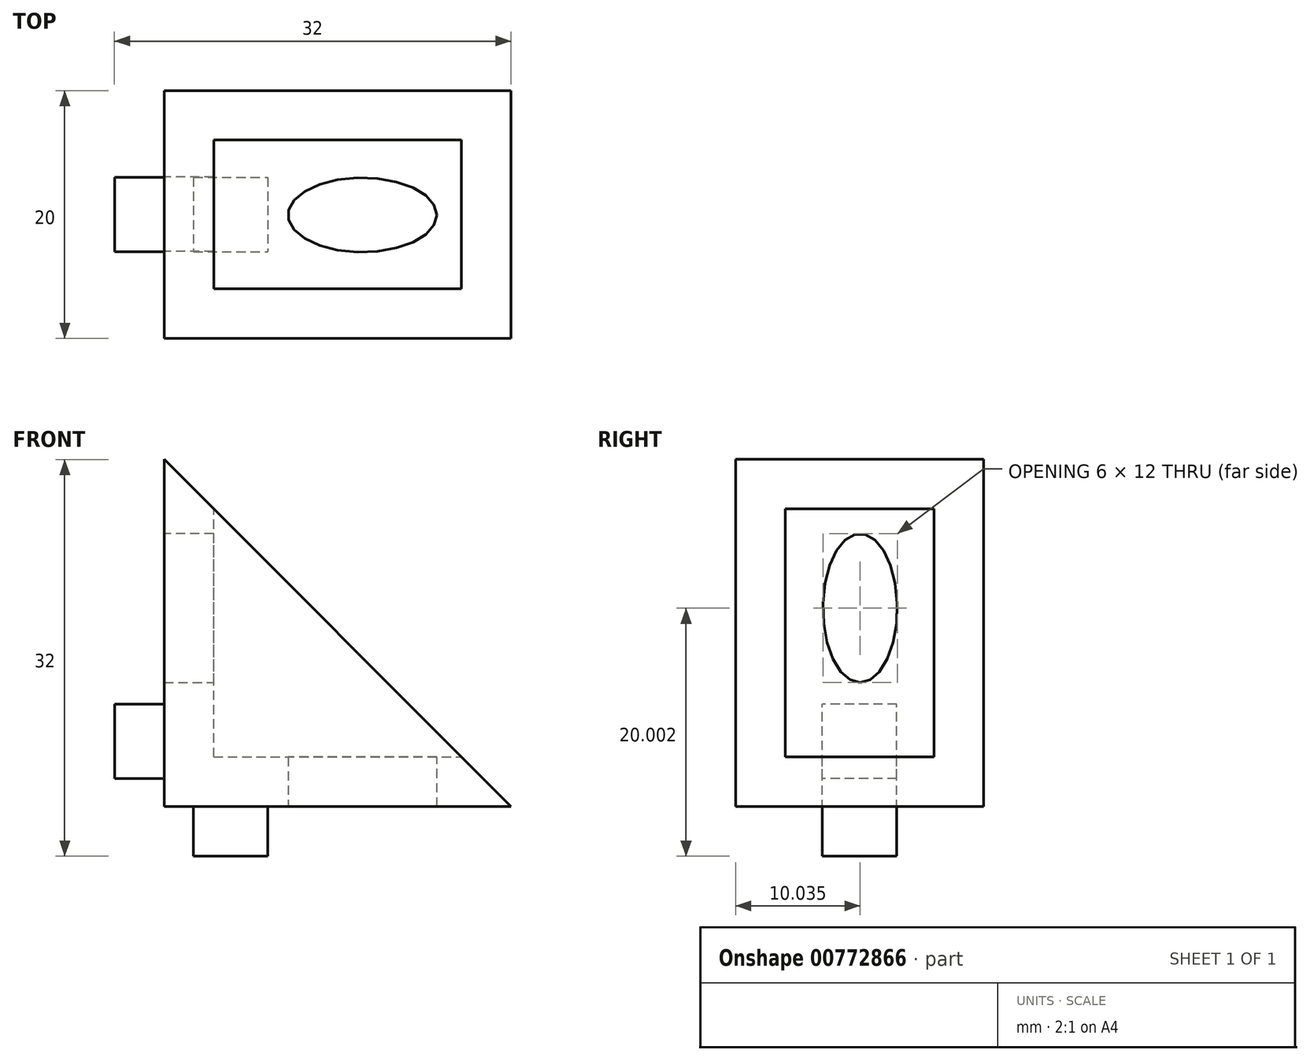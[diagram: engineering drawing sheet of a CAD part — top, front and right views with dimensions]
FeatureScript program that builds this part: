
annotation { "Feature Type Name" : "Feature", "Feature Type Description" : "" }
export const myFeature = defineFeature(function(context is Context, id is Id, definition is map)
    precondition{}
    {
        {
            var Q0;
            Q0=qCreatedBy(makeId("Front.planeOp"),FACE);
            var sketch = newSketch(context, id + "F0", { "sketchPlane" : qUnion([Q0])});
            skLineSegment(sketch, "E0.bottom", {"start": v(-14.58, 14.66) * mm, "end": v(13.42, 14.66) * mm});
            skLineSegment(sketch, "E0.top", {"start": v(-14.58, -13.34) * mm, "end": v(13.42, -13.34) * mm});
            skLineSegment(sketch, "E0.left", {"start": v(-14.58, 14.66) * mm, "end": v(-14.58, -13.34) * mm});
            skLineSegment(sketch, "E0.right", {"start": v(13.42, 14.66) * mm, "end": v(13.42, -13.34) * mm});
            skSolve(sketch);
        }
        {
            var Q0;
            Q0 = qSketchRegion(id + "F0", true);
            extrude(context, id + "F1", {"entities" : qUnion([Q0]), "depth" : 20 * mm, "offsetDistance" : 25 * mm});
        }
        {
            var Q0;
            Q0=makeQuery(id+"F1.opExtrude","SWEPT_FACE",FACE,{"disambiguationData":[OSD([sQuery(id+"F0.wireOp",EDGE,"E0.bottom")])]});
            var sketch = newSketch(context, id + "F2", { "sketchPlane" : qUnion([Q0])});
            skLineSegment(sketch, "E1.bottom", {"start": v(-10.58, -16) * mm, "end": v(9.42, -16) * mm});
            skLineSegment(sketch, "E1.top", {"start": v(-10.58, -4) * mm, "end": v(9.42, -4) * mm});
            skLineSegment(sketch, "E1.left", {"start": v(-10.58, -16) * mm, "end": v(-10.58, -4) * mm});
            skLineSegment(sketch, "E1.right", {"start": v(9.42, -16) * mm, "end": v(9.42, -4) * mm});
            skSolve(sketch);
        }
        {
            var Q0;
            Q0 = qSketchRegion(id + "F2", true);
            extrude(context, id + "F3", {"entities" : qUnion([Q0]), "operationType" : NewBodyOperationType.REMOVE, "oppositeDirection" : true, "depth" : 24 * mm, "offsetDistance" : 25 * mm});
        }
        {
            var Q0;
            Q0=makeQuery(id+"F1.opExtrude","SWEPT_FACE",FACE,{"disambiguationData":[OSD([sQuery(id+"F0.wireOp",EDGE,"E0.right")])]});
            var sketch = newSketch(context, id + "F4", { "sketchPlane" : qUnion([Q0])});
            skLineSegment(sketch, "E2.bottom", {"start": v(-16, 10.66) * mm, "end": v(-4, 10.66) * mm});
            skLineSegment(sketch, "E2.top", {"start": v(-16, -9.34) * mm, "end": v(-4, -9.34) * mm});
            skLineSegment(sketch, "E2.left", {"start": v(-16, 10.66) * mm, "end": v(-16, -9.34) * mm});
            skLineSegment(sketch, "E2.right", {"start": v(-4, 10.66) * mm, "end": v(-4, -9.34) * mm});
            skSolve(sketch);
        }
        {
            var Q0;
            Q0 = qSketchRegion(id + "F4", true);
            extrude(context, id + "F5", {"entities" : qUnion([Q0]), "operationType" : NewBodyOperationType.REMOVE, "oppositeDirection" : true, "depth" : 24 * mm, "offsetDistance" : 25 * mm});
        }
        {
            var Q0;
            Q0=makeQuery(id+"F1.opExtrude","CAP_FACE",FACE,{"disambiguationData":[OSD([sQuery(id+"F0.wireOp",EDGE,"E0.bottom"),sQuery(id+"F0.wireOp",EDGE,"E0.top"),sQuery(id+"F0.wireOp",EDGE,"E0.left"),sQuery(id+"F0.wireOp",EDGE,"E0.right")])],"isStart":false});
            var sketch = newSketch(context, id + "F6", { "sketchPlane" : qUnion([Q0])});
            skLineSegment(sketch, "E3", {"start": v(-14.58, 14.66) * mm, "end": v(13.42, -13.34) * mm});
            skLineSegment(sketch, "E4", {"start": v(13.42, -13.34) * mm, "end": v(13.42, 14.66) * mm});
            skLineSegment(sketch, "E5", {"start": v(13.42, 14.66) * mm, "end": v(-14.58, 14.66) * mm});
            skSolve(sketch);
        }
        {
            var Q0;
            Q0 = qSketchRegion(id + "F6", true);
            extrude(context, id + "F7", {"entities" : qUnion([Q0]), "operationType" : NewBodyOperationType.REMOVE, "endBound" : BoundingType.THROUGH_ALL, "oppositeDirection" : true, "depth" : 25 * mm, "offsetDistance" : 25 * mm});
        }
        {
            var Q0;
            Q0=makeQuery(id+"F5.boolean.opBoolean","MERGE",FACE,{"derivedFrom":[makeQuery(id+"F3.boolean.opBoolean","COPY",FACE,{"derivedFrom":makeQuery(id+"F3.opExtrude","CAP_FACE",FACE,{"disambiguationData":[OSD([sQuery(id+"F2.wireOp",EDGE,"E1.bottom"),sQuery(id+"F2.wireOp",EDGE,"E1.top"),sQuery(id+"F2.wireOp",EDGE,"E1.left"),sQuery(id+"F2.wireOp",EDGE,"E1.right")])],"isStart":false})}),makeQuery(id+"F5.opExtrude","SWEPT_FACE",FACE,{"disambiguationData":[OSD([sQuery(id+"F4.wireOp",EDGE,"E2.top")])]})]});
            var sketch = newSketch(context, id + "F8", { "sketchPlane" : qUnion([Q0])});
            skEllipse(sketch, "E6", {"center": v(1.42, -10.03) * mm, "majorRadius": 6 * mm, "minorRadius": 3 * mm, "majorAxis": v(1, 0)});
            skSolve(sketch);
        }
        {
            var Q0;
            Q0 = qSketchRegion(id + "F8", true);
            extrude(context, id + "F9", {"entities" : qUnion([Q0]), "operationType" : NewBodyOperationType.REMOVE, "endBound" : BoundingType.THROUGH_ALL, "oppositeDirection" : true, "depth" : 25 * mm, "offsetDistance" : 25 * mm});
        }
        {
            var Q0;
            Q0=makeQuery(id+"F3.boolean.opBoolean","COPY",FACE,{"derivedFrom":makeQuery(id+"F3.opExtrude","SWEPT_FACE",FACE,{"disambiguationData":[OSD([sQuery(id+"F2.wireOp",EDGE,"E1.left")])]})});
            var sketch = newSketch(context, id + "F10", { "sketchPlane" : qUnion([Q0])});
            skEllipse(sketch, "E7", {"center": v(-9.97, 2.66) * mm, "majorRadius": 6 * mm, "minorRadius": 3 * mm, "majorAxis": v(0, -1)});
            skSolve(sketch);
        }
        {
            var Q0;
            Q0 = qSketchRegion(id + "F10", true);
            extrude(context, id + "F11", {"entities" : qUnion([Q0]), "operationType" : NewBodyOperationType.REMOVE, "endBound" : BoundingType.THROUGH_ALL, "oppositeDirection" : true, "depth" : 25 * mm, "offsetDistance" : 25 * mm});
        }
        {
            var Q0;
            Q0=makeQuery(id+"F1.opExtrude","SWEPT_FACE",FACE,{"disambiguationData":[OSD([sQuery(id+"F0.wireOp",EDGE,"E0.left")])]});
            var sketch = newSketch(context, id + "F12", { "sketchPlane" : qUnion([Q0])});
            skLineSegment(sketch, "E8.bottom", {"start": v(7, -11.06) * mm, "end": v(13, -11.06) * mm});
            skLineSegment(sketch, "E8.top", {"start": v(7, -5.06) * mm, "end": v(13, -5.06) * mm});
            skLineSegment(sketch, "E8.left", {"start": v(7, -11.06) * mm, "end": v(7, -5.06) * mm});
            skLineSegment(sketch, "E8.right", {"start": v(13, -11.06) * mm, "end": v(13, -5.06) * mm});
            skSolve(sketch);
        }
        {
            var Q0;
            Q0=makeQuery(id+"F12.imprint","IMPRINT",FACE,{"disambiguationData":[TD([[makeQuery(id+"F12.imprint","IMPRINT",EDGE,{"derivedFrom":sQuery(id+"F12.wireOp",EDGE,"E8.bottom")}),1.0]])]});
            extrude(context, id + "F13", {"entities" : qUnion([Q0]), "operationType" : NewBodyOperationType.ADD, "depth" : 4 * mm, "offsetDistance" : 25 * mm});
        }
        {
            var Q0;
            Q0=makeQuery(id+"F1.opExtrude","SWEPT_FACE",FACE,{"disambiguationData":[OSD([sQuery(id+"F0.wireOp",EDGE,"E0.top")])]});
            var sketch = newSketch(context, id + "F14", { "sketchPlane" : qUnion([Q0])});
            skLineSegment(sketch, "E9.bottom", {"start": v(-12.2, 7) * mm, "end": v(-6.2, 7) * mm});
            skLineSegment(sketch, "E9.top", {"start": v(-12.2, 13) * mm, "end": v(-6.2, 13) * mm});
            skLineSegment(sketch, "E9.left", {"start": v(-12.2, 7) * mm, "end": v(-12.2, 13) * mm});
            skLineSegment(sketch, "E9.right", {"start": v(-6.2, 7) * mm, "end": v(-6.2, 13) * mm});
            skSolve(sketch);
        }
        {
            var Q0;
            Q0 = qSketchRegion(id + "F14", true);
            extrude(context, id + "F15", {"entities" : qUnion([Q0]), "operationType" : NewBodyOperationType.ADD, "depth" : 4 * mm, "offsetDistance" : 25 * mm});
        }
    });
